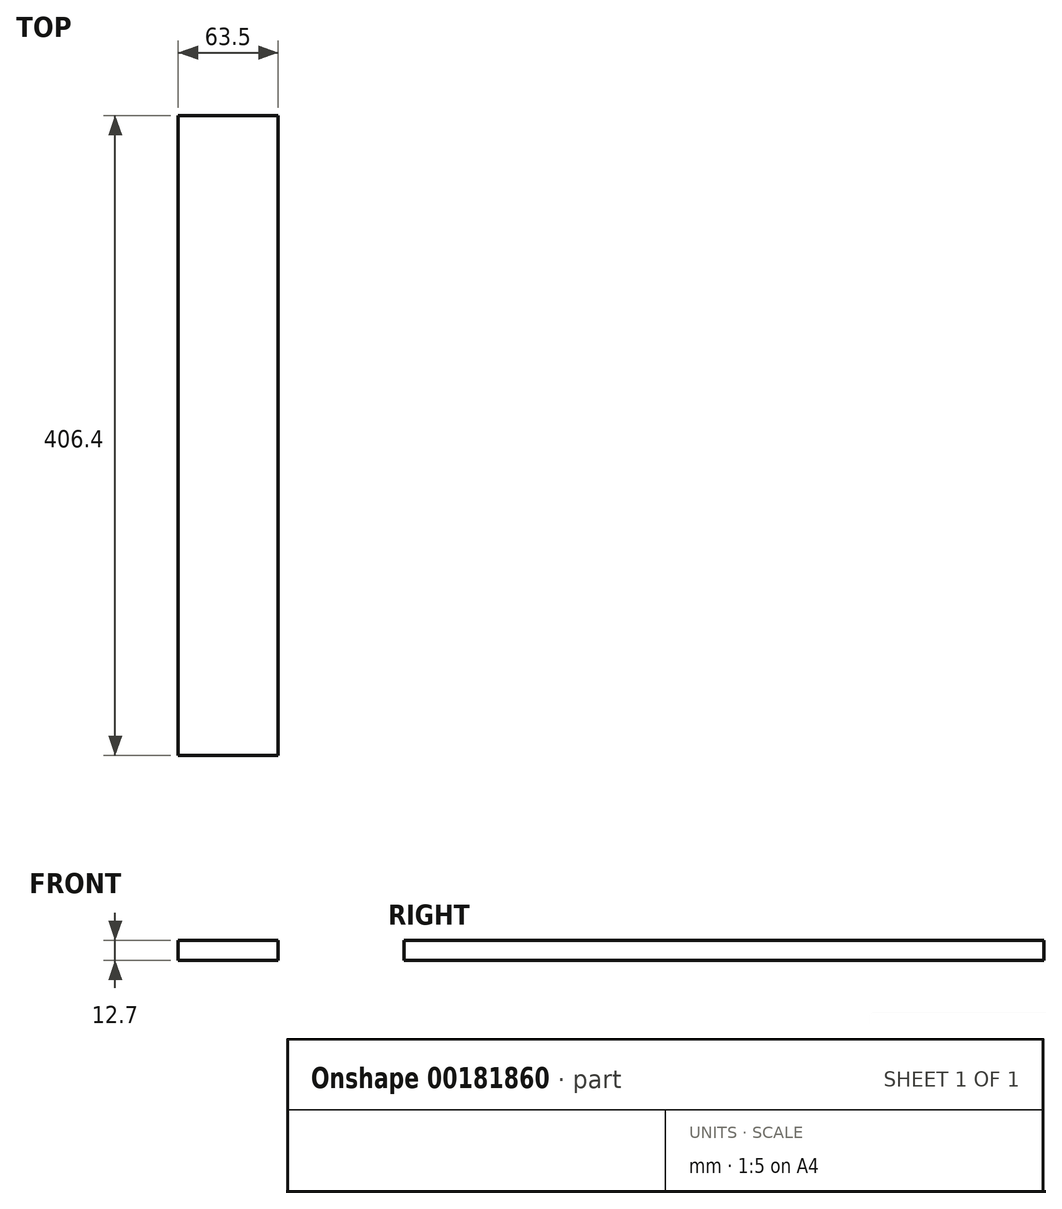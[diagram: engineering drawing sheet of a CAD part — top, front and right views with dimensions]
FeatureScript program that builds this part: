
annotation { "Feature Type Name" : "Feature", "Feature Type Description" : "" }
export const myFeature = defineFeature(function(context is Context, id is Id, definition is map)
    precondition{}
    {
        {
            var Q0;
            Q0=qCreatedBy(makeId("Front.planeOp"),FACE);
            var sketch = newSketch(context, id + "F0", { "sketchPlane" : qUnion([Q0])});
            skLineSegment(sketch, "E0.bottom", {"start": v(0, 0) * mm, "end": v(63.5, 0) * mm});
            skLineSegment(sketch, "E0.top", {"start": v(0, 12.7) * mm, "end": v(63.5, 12.7) * mm});
            skLineSegment(sketch, "E0.left", {"start": v(0, 0) * mm, "end": v(0, 12.7) * mm});
            skLineSegment(sketch, "E0.right", {"start": v(63.5, 0) * mm, "end": v(63.5, 12.7) * mm});
            skLineSegment(sketch, "E1.bottom", {"start": v(-5.13, 3.95) * mm, "end": v(-5.55, 3.95) * mm});
            skLineSegment(sketch, "E1.top", {"start": v(-5.13, 49.25) * mm, "end": v(-5.55, 49.25) * mm});
            skSolve(sketch);
        }
        {
            var Q0;
            Q0 = qSketchRegion(id + "F0", true);
            extrude(context, id + "F1", {"entities" : qUnion([Q0]), "depth" : 406.4 * mm});
        }
    });
